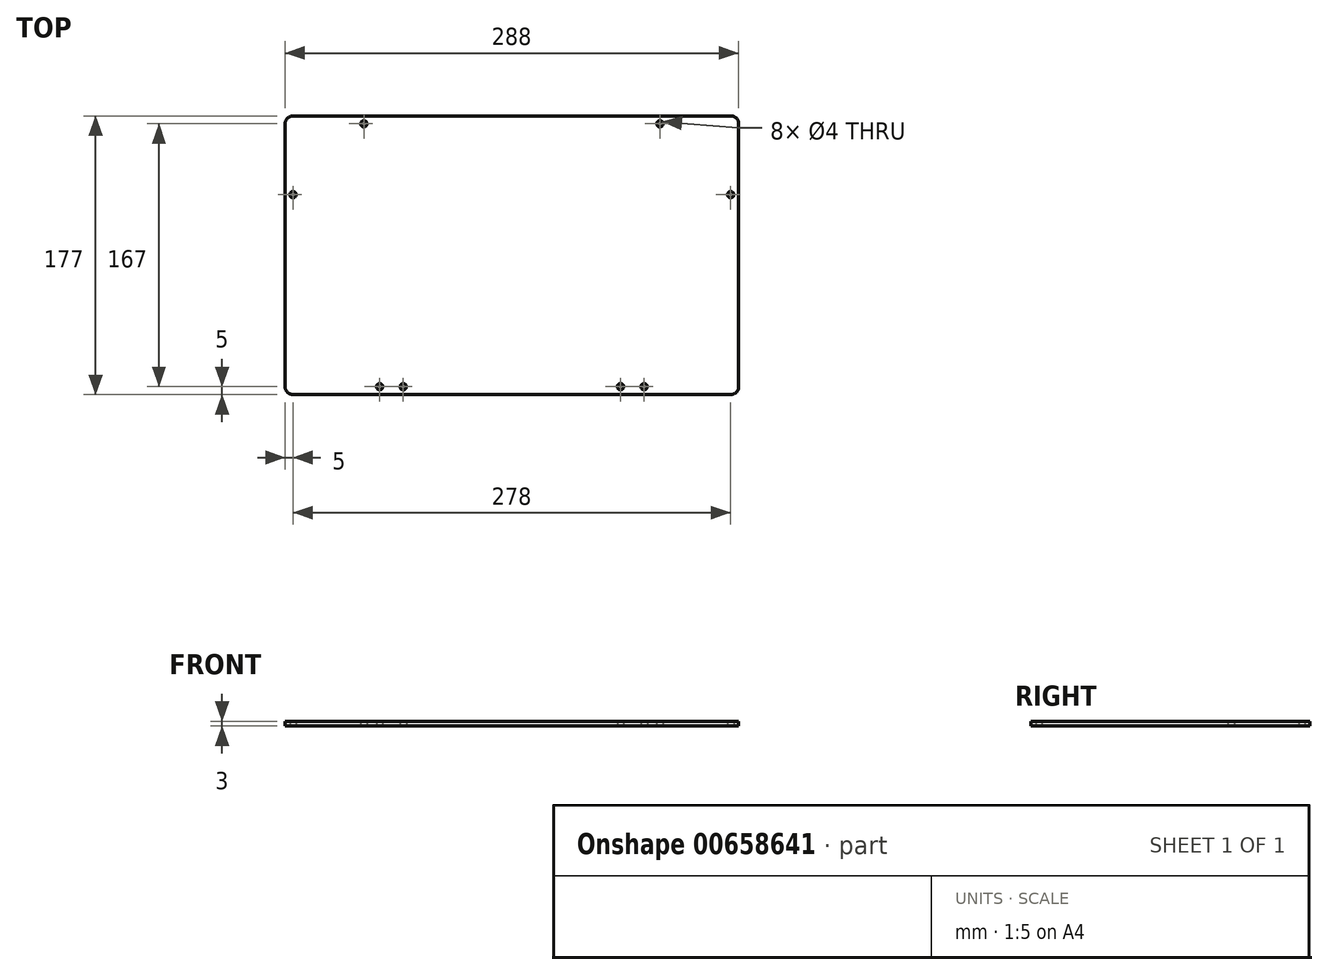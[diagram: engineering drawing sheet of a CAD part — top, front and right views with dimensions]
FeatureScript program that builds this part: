
annotation { "Feature Type Name" : "Feature", "Feature Type Description" : "" }
export const myFeature = defineFeature(function(context is Context, id is Id, definition is map)
    precondition{}
    {
        {
            var Q0;
            Q0=qCreatedBy(makeId("Top.planeOp"),FACE);
            var sketch = newSketch(context, id + "F0", { "sketchPlane" : qUnion([Q0])});
            skLineSegment(sketch, "E0.bottom", {"start": v(-144, 96) * mm, "end": v(144, 96) * mm});
            skLineSegment(sketch, "E0.top", {"start": v(-144, -81) * mm, "end": v(144, -81) * mm});
            skLineSegment(sketch, "E0.left", {"start": v(-144, 96) * mm, "end": v(-144, -81) * mm});
            skLineSegment(sketch, "E0.right", {"start": v(144, 96) * mm, "end": v(144, -81) * mm});
            skCircle(sketch, "E1", {"center": v(-94, 91) * mm, "radius": 2 * mm});
            skCircle(sketch, "E2", {"center": v(-139, 46) * mm, "radius": 2 * mm});
            skCircle(sketch, "E3", {"center": v(94, 91) * mm, "radius": 2 * mm});
            skCircle(sketch, "E4", {"center": v(139, 46) * mm, "radius": 2 * mm});
            skCircle(sketch, "E5", {"center": v(-84, -76) * mm, "radius": 2 * mm});
            skCircle(sketch, "E6", {"center": v(-69, -76) * mm, "radius": 2 * mm});
            skCircle(sketch, "E7", {"center": v(84, -76) * mm, "radius": 2 * mm});
            skCircle(sketch, "E8", {"center": v(69, -76) * mm, "radius": 2 * mm});
            skSolve(sketch);
        }
        {
            var Q0;
            Q0=makeQuery(id+"F0.imprint","IMPRINT",FACE,{"disambiguationData":[TD([[makeQuery(id+"F0.imprint","IMPRINT",EDGE,{"derivedFrom":sQuery(id+"F0.wireOp",EDGE,"E0.bottom")}),-1.0]])]});
            extrude(context, id + "F1", {"entities" : qUnion([Q0]), "depth" : 3 * mm, "offsetDistance" : 25 * mm});
        }
        {
            var Q0;
            Q0=makeQuery(id+"F1.opExtrude","SWEPT_EDGE",EDGE,{"disambiguationData":[OSD([sQuery(id+"F0.wireOp",EDGE,"E0.bottom"),sQuery(id+"F0.wireOp",EDGE,"E0.left")])]});
            var Q1;
            Q1=makeQuery(id+"F1.opExtrude","SWEPT_EDGE",EDGE,{"disambiguationData":[OSD([sQuery(id+"F0.wireOp",EDGE,"E0.bottom"),sQuery(id+"F0.wireOp",EDGE,"E0.right")])]});
            var Q2;
            Q2=makeQuery(id+"F1.opExtrude","SWEPT_EDGE",EDGE,{"disambiguationData":[OSD([sQuery(id+"F0.wireOp",EDGE,"E0.top"),sQuery(id+"F0.wireOp",EDGE,"E0.right")])]});
            var Q3;
            Q3=makeQuery(id+"F1.opExtrude","SWEPT_EDGE",EDGE,{"disambiguationData":[OSD([sQuery(id+"F0.wireOp",EDGE,"E0.top"),sQuery(id+"F0.wireOp",EDGE,"E0.left")])]});
            fillet(context, id + "F2", {"entities" : qUnion([Q0, Q1, Q2, Q3]), "radius" : 5 * mm, "tangentPropagation" : true, "allowEdgeOverflow" : false});
        }
    });
